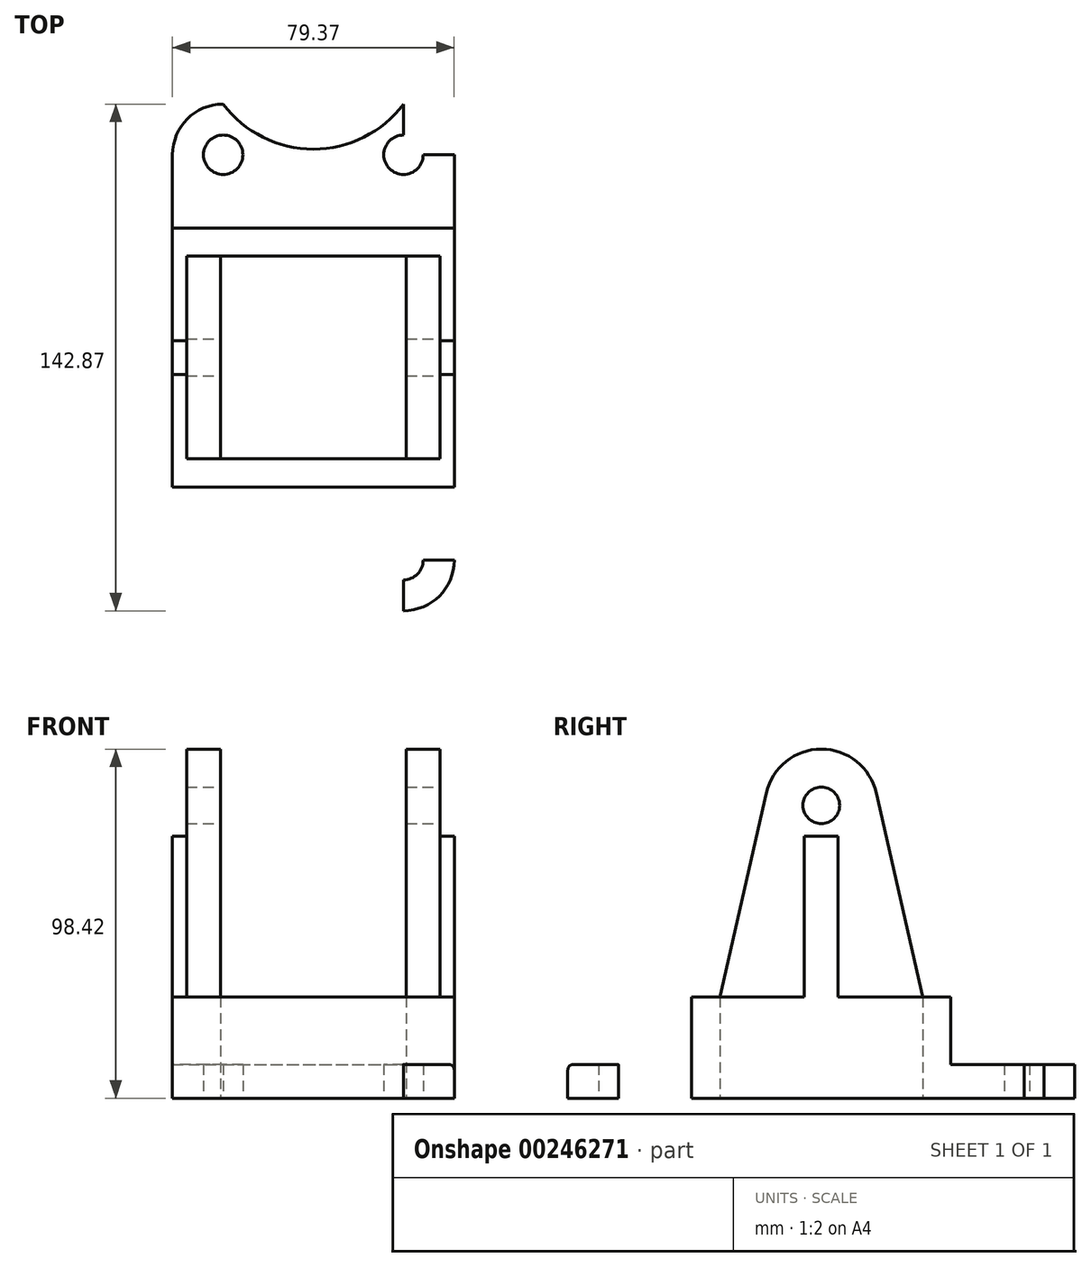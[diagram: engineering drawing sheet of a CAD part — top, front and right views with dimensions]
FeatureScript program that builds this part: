
annotation { "Feature Type Name" : "Feature", "Feature Type Description" : "" }
export const myFeature = defineFeature(function(context is Context, id is Id, definition is map)
    precondition{}
    {
        {
            var Q0;
            Q0=qCreatedBy(makeId("Top.planeOp"),FACE);
            var sketch = newSketch(context, id + "F0", { "sketchPlane" : qUnion([Q0])});
            skArc(sketch, "E0", {"start": v(-23.97, 73.31) * mm, "mid": v(-34.08, 69.13) * mm, "end": v(-38.26, 59.03) * mm});
            skLineSegment(sketch, "E1", {"start": v(-23.97, 59.03) * mm, "end": v(-23.97, 73.31) * mm, "construction": true});
            skLineSegment(sketch, "E2", {"start": v(-23.97, 59.03) * mm, "end": v(-38.26, 59.03) * mm, "construction": true});
            skLineSegment(sketch, "E3", {"start": v(-38.26, 59.03) * mm, "end": v(-38.26, -55.27) * mm});
            skLineSegment(sketch, "E4", {"start": v(-23.97, 73.31) * mm, "end": v(26.83, 73.31) * mm, "construction": true});
            skPoint(sketch, "E5", {"position": v(1.43, 73.31) * mm});
            skArc(sketch, "E6", {"start": v(-23.97, 73.31) * mm, "mid": v(1.43, 60.61) * mm, "end": v(26.83, 73.31) * mm});
            skCircle(sketch, "E7", {"center": v(-23.97, 59.03) * mm, "radius": 5.56 * mm});
            skPoint(sketch, "E8", {"position": v(-38.26, 1.88) * mm});
            skLineSegment(sketch, "E9.MirrorCS", {"start": v(-23.97, -69.56) * mm, "end": v(26.83, -69.56) * mm, "construction": true});
            skArc(sketch, "E10.MirrorCS", {"start": v(-23.97, -69.56) * mm, "mid": v(1.43, -56.86) * mm, "end": v(26.83, -69.56) * mm});
            skArc(sketch, "E11.MirrorC", {"start": v(-23.97, -69.56) * mm, "mid": v(-34.08, -65.38) * mm, "end": v(-38.26, -55.27) * mm});
            skLineSegment(sketch, "E12.MirrorCS", {"start": v(-23.97, -55.27) * mm, "end": v(-38.26, -55.27) * mm, "construction": true});
            skCircle(sketch, "E13.MirrorC", {"center": v(-23.97, -55.27) * mm, "radius": 5.56 * mm});
            skLineSegment(sketch, "E14.MirrorCS", {"start": v(-23.97, -55.27) * mm, "end": v(-23.97, -69.56) * mm, "construction": true});
            skPoint(sketch, "E15.MirrorP", {"position": v(1.43, -69.56) * mm});
            skLineSegment(sketch, "E16", {"start": v(-38.26, 1.88) * mm, "end": v(-34.3, 1.88) * mm, "construction": true});
            skLineSegment(sketch, "E17", {"start": v(-34.3, 6.64) * mm, "end": v(-34.3, -2.89) * mm});
            skPoint(sketch, "E18", {"position": v(-34.3, 1.88) * mm});
            skLineSegment(sketch, "E19", {"start": v(-34.3, 6.64) * mm, "end": v(-38.26, 6.64) * mm});
            skLineSegment(sketch, "E20", {"start": v(-34.3, -2.89) * mm, "end": v(-38.26, -2.89) * mm});
            skLineSegment(sketch, "E21", {"start": v(1.43, 73.31) * mm, "end": v(1.43, -69.56) * mm, "construction": true});
            skLineSegment(sketch, "E22", {"start": v(-34.3, 1.88) * mm, "end": v(-34.3, 30.45) * mm, "construction": true});
            skLineSegment(sketch, "E23", {"start": v(-38.26, 30.45) * mm, "end": v(1.43, 30.45) * mm});
            skLineSegment(sketch, "E24", {"start": v(-38.26, 38.39) * mm, "end": v(1.43, 38.39) * mm});
            skLineSegment(sketch, "E25.MirrorCS", {"start": v(37.14, -2.89) * mm, "end": v(41.11, -2.89) * mm});
            skLineSegment(sketch, "E26.MirrorCS", {"start": v(41.11, 1.88) * mm, "end": v(37.14, 1.88) * mm, "construction": true});
            skLineSegment(sketch, "E27.MirrorCS", {"start": v(37.14, 6.64) * mm, "end": v(37.14, -2.89) * mm});
            skLineSegment(sketch, "E28.MirrorCS", {"start": v(37.14, 6.64) * mm, "end": v(41.11, 6.64) * mm});
            skLineSegment(sketch, "E29.MirrorCS", {"start": v(37.14, 1.88) * mm, "end": v(37.14, 30.45) * mm, "construction": true});
            skCircle(sketch, "E30.MirrorC", {"center": v(26.83, -55.27) * mm, "radius": 5.56 * mm});
            skLineSegment(sketch, "E31.MirrorCS", {"start": v(26.83, -55.27) * mm, "end": v(41.11, -55.27) * mm});
            skLineSegment(sketch, "E32.MirrorCS", {"start": v(41.11, 38.39) * mm, "end": v(1.43, 38.39) * mm});
            skCircle(sketch, "E33.MirrorC", {"center": v(26.83, 59.03) * mm, "radius": 5.56 * mm});
            skArc(sketch, "E34.MirrorCS", {"start": v(26.83, -69.56) * mm, "mid": v(36.93, -65.38) * mm, "end": v(41.11, -55.27) * mm});
            skLineSegment(sketch, "E35.MirrorCS", {"start": v(41.11, 30.45) * mm, "end": v(1.43, 30.45) * mm});
            skPoint(sketch, "E36.MirrorP", {"position": v(41.11, 1.88) * mm});
            skLineSegment(sketch, "E37.MirrorCS", {"start": v(26.83, -55.27) * mm, "end": v(26.83, -69.56) * mm});
            skPoint(sketch, "E38.MirrorP", {"position": v(37.14, 1.88) * mm});
            skArc(sketch, "E39.MirrorCS", {"start": v(26.83, 73.31) * mm, "mid": v(36.93, 69.13) * mm, "end": v(41.11, 59.03) * mm});
            skLineSegment(sketch, "E40.MirrorCS", {"start": v(26.83, 59.03) * mm, "end": v(26.83, 73.31) * mm});
            skLineSegment(sketch, "E41.MirrorCS", {"start": v(26.83, 59.03) * mm, "end": v(41.11, 59.03) * mm});
            skLineSegment(sketch, "E42.MirrorCS", {"start": v(41.11, 59.03) * mm, "end": v(41.11, -55.27) * mm});
            skLineSegment(sketch, "E43", {"start": v(-34.3, -2.89) * mm, "end": v(-34.3, -26.7) * mm, "construction": true});
            skLineSegment(sketch, "E44", {"start": v(-38.26, -26.7) * mm, "end": v(41.11, -26.7) * mm});
            skLineSegment(sketch, "E45", {"start": v(-38.26, -34.64) * mm, "end": v(41.11, -34.64) * mm});
            skLineSegment(sketch, "E46", {"start": v(-34.3, 38.39) * mm, "end": v(-34.3, -34.64) * mm});
            skLineSegment(sketch, "E47", {"start": v(-24.77, 38.39) * mm, "end": v(-24.77, -34.64) * mm});
            skLineSegment(sketch, "E48", {"start": v(37.14, 38.39) * mm, "end": v(37.14, -34.64) * mm});
            skLineSegment(sketch, "E49", {"start": v(27.62, 38.39) * mm, "end": v(27.62, -34.64) * mm});
            skSolve(sketch);
        }
        {
            var Q0;
            {var subQ1=sQuery(id+"F0.wireOp",EDGE,"E23");var subQ5=sQuery(id+"F0.wireOp",EDGE,"E3");var subQ7=makeQuery(id+"F0.imprint","INTERSECT",VERTEX,{"derivedFrom":[subQ5,subQ1]});Q0=makeQuery(id+"F0.imprint","IMPRINT",FACE,{"disambiguationData":[TD([[makeQuery(id+"F0.imprint","IMPRINT",EDGE,{"disambiguationData":[TD([[subQ7,1.0]])],"derivedFrom":subQ5}),1.0]])]});}
            var Q1;
            {var subQ5=sQuery(id+"F0.wireOp",EDGE,"E19");Q1=makeQuery(id+"F0.imprint","IMPRINT",FACE,{"disambiguationData":[TD([[makeQuery(id+"F0.imprint","IMPRINT",EDGE,{"derivedFrom":subQ5}),-1.0]])]});}
            var Q2;
            {var subQ3=sQuery(id+"F0.wireOp",EDGE,"E35.MirrorCS");var subQ7=sQuery(id+"F0.wireOp",EDGE,"E23");var subQ9=makeQuery(id+"F0.imprint","INTERSECT",VERTEX,{"derivedFrom":[subQ7,subQ3]});Q2=makeQuery(id+"F0.imprint","IMPRINT",FACE,{"disambiguationData":[TD([[makeQuery(id+"F0.imprint","IMPRINT",EDGE,{"disambiguationData":[TD([[subQ9,1.0]])],"derivedFrom":subQ7}),-1.0]])]});}
            var Q3;
            {var subQ3=sQuery(id+"F0.wireOp",EDGE,"E25.MirrorCS");Q3=makeQuery(id+"F0.imprint","IMPRINT",FACE,{"disambiguationData":[TD([[makeQuery(id+"F0.imprint","IMPRINT",EDGE,{"derivedFrom":subQ3}),-1.0]])]});}
            var Q4;
            {var subQ3=sQuery(id+"F0.wireOp",EDGE,"E20");Q4=makeQuery(id+"F0.imprint","IMPRINT",FACE,{"disambiguationData":[TD([[makeQuery(id+"F0.imprint","IMPRINT",EDGE,{"derivedFrom":subQ3}),1.0]])]});}
            var Q5;
            {var subQ1=sQuery(id+"F0.wireOp",EDGE,"E44");var subQ5=sQuery(id+"F0.wireOp",EDGE,"E3");var subQ7=makeQuery(id+"F0.imprint","INTERSECT",VERTEX,{"derivedFrom":[subQ5,subQ1]});Q5=makeQuery(id+"F0.imprint","IMPRINT",FACE,{"disambiguationData":[TD([[makeQuery(id+"F0.imprint","IMPRINT",EDGE,{"disambiguationData":[TD([[subQ7,-1.0]])],"derivedFrom":subQ5}),1.0]])]});}
            var Q6;
            {var subQ3=sQuery(id+"F0.wireOp",EDGE,"E28.MirrorCS");Q6=makeQuery(id+"F0.imprint","IMPRINT",FACE,{"disambiguationData":[TD([[makeQuery(id+"F0.imprint","IMPRINT",EDGE,{"derivedFrom":subQ3}),1.0]])]});}
            var Q7;
            {var subQ0=sQuery(id+"F0.wireOp",EDGE,"E42.MirrorCS");var subQ3=sQuery(id+"F0.wireOp",EDGE,"E32.MirrorCS");var subQ4=makeQuery(id+"F0.imprint","INTERSECT",VERTEX,{"derivedFrom":[subQ3,subQ0]});Q7=makeQuery(id+"F0.imprint","IMPRINT",FACE,{"disambiguationData":[TD([[makeQuery(id+"F0.imprint","IMPRINT",EDGE,{"disambiguationData":[TD([[subQ4,-1.0]])],"derivedFrom":subQ3}),1.0]])]});}
            var Q8;
            {var subQ1=sQuery(id+"F0.wireOp",EDGE,"E44");var subQ5=sQuery(id+"F0.wireOp",EDGE,"E46");var subQ6=makeQuery(id+"F0.imprint","INTERSECT",VERTEX,{"derivedFrom":[subQ1,subQ5]});Q8=makeQuery(id+"F0.imprint","IMPRINT",FACE,{"disambiguationData":[TD([[makeQuery(id+"F0.imprint","IMPRINT",EDGE,{"disambiguationData":[TD([[subQ6,-1.0]])],"derivedFrom":subQ1}),-1.0]])]});}
            var Q9;
            {var subQ1=sQuery(id+"F0.wireOp",EDGE,"E44");var subQ5=sQuery(id+"F0.wireOp",EDGE,"E47");var subQ6=makeQuery(id+"F0.imprint","INTERSECT",VERTEX,{"derivedFrom":[subQ1,subQ5]});Q9=makeQuery(id+"F0.imprint","IMPRINT",FACE,{"disambiguationData":[TD([[makeQuery(id+"F0.imprint","IMPRINT",EDGE,{"disambiguationData":[TD([[subQ6,-1.0]])],"derivedFrom":subQ1}),-1.0]])]});}
            var Q10;
            {var subQ3=sQuery(id+"F0.wireOp",EDGE,"E32.MirrorCS");var subQ5=sQuery(id+"F0.wireOp",EDGE,"E48");var subQ7=makeQuery(id+"F0.imprint","INTERSECT",VERTEX,{"derivedFrom":[subQ3,subQ5]});Q10=makeQuery(id+"F0.imprint","IMPRINT",FACE,{"disambiguationData":[TD([[makeQuery(id+"F0.imprint","IMPRINT",EDGE,{"disambiguationData":[TD([[subQ7,-1.0]])],"derivedFrom":subQ3}),1.0]])]});}
            var Q11;
            {var subQ3=sQuery(id+"F0.wireOp",EDGE,"E42.MirrorCS");var subQ5=sQuery(id+"F0.wireOp",EDGE,"E44");var subQ7=makeQuery(id+"F0.imprint","INTERSECT",VERTEX,{"derivedFrom":[subQ3,subQ5]});Q11=makeQuery(id+"F0.imprint","IMPRINT",FACE,{"disambiguationData":[TD([[makeQuery(id+"F0.imprint","IMPRINT",EDGE,{"disambiguationData":[TD([[subQ7,-1.0]])],"derivedFrom":subQ3}),-1.0]])]});}
            var Q12;
            {var subQ0=sQuery(id+"F0.wireOp",EDGE,"E49");var subQ1=sQuery(id+"F0.wireOp",EDGE,"E44");var subQ2=makeQuery(id+"F0.imprint","INTERSECT",VERTEX,{"derivedFrom":[subQ1,subQ0]});Q12=makeQuery(id+"F0.imprint","IMPRINT",FACE,{"disambiguationData":[TD([[makeQuery(id+"F0.imprint","IMPRINT",EDGE,{"disambiguationData":[TD([[subQ2,-1.0]])],"derivedFrom":subQ1}),-1.0]])]});}
            var Q13;
            {var subQ1=sQuery(id+"F0.wireOp",EDGE,"E23");var subQ5=sQuery(id+"F0.wireOp",EDGE,"E46");var subQ6=makeQuery(id+"F0.imprint","INTERSECT",VERTEX,{"derivedFrom":[subQ1,subQ5]});Q13=makeQuery(id+"F0.imprint","IMPRINT",FACE,{"disambiguationData":[TD([[makeQuery(id+"F0.imprint","IMPRINT",EDGE,{"disambiguationData":[TD([[subQ6,-1.0]])],"derivedFrom":subQ1}),1.0]])]});}
            var Q14;
            {var subQ3=sQuery(id+"F0.wireOp",EDGE,"E35.MirrorCS");var subQ5=sQuery(id+"F0.wireOp",EDGE,"E48");var subQ9=makeQuery(id+"F0.imprint","INTERSECT",VERTEX,{"derivedFrom":[subQ3,subQ5]});Q14=makeQuery(id+"F0.imprint","IMPRINT",FACE,{"disambiguationData":[TD([[makeQuery(id+"F0.imprint","IMPRINT",EDGE,{"disambiguationData":[TD([[subQ9,-1.0]])],"derivedFrom":subQ3}),1.0]])]});}
            var Q15;
            {var subQ3=sQuery(id+"F0.wireOp",EDGE,"E23");var subQ5=sQuery(id+"F0.wireOp",EDGE,"E46");var subQ9=makeQuery(id+"F0.imprint","INTERSECT",VERTEX,{"derivedFrom":[subQ3,subQ5]});Q15=makeQuery(id+"F0.imprint","IMPRINT",FACE,{"disambiguationData":[TD([[makeQuery(id+"F0.imprint","IMPRINT",EDGE,{"disambiguationData":[TD([[subQ9,-1.0]])],"derivedFrom":subQ3}),-1.0]])]});}
            var Q16;
            {var subQ1=sQuery(id+"F0.wireOp",EDGE,"E35.MirrorCS");var subQ6=sQuery(id+"F0.wireOp",EDGE,"E23");var subQ10=makeQuery(id+"F0.imprint","INTERSECT",VERTEX,{"derivedFrom":[subQ6,subQ1]});Q16=makeQuery(id+"F0.imprint","IMPRINT",FACE,{"disambiguationData":[TD([[makeQuery(id+"F0.imprint","IMPRINT",EDGE,{"disambiguationData":[TD([[subQ10,1.0]])],"derivedFrom":subQ6}),1.0]])]});}
            var Q17;
            {var subQ19=sQuery(id+"F0.wireOp",EDGE,"E0");Q17=makeQuery(id+"F0.imprint","IMPRINT",FACE,{"disambiguationData":[TD([[makeQuery(id+"F0.imprint","IMPRINT",EDGE,{"derivedFrom":subQ19}),1.0]])]});}
            var Q18;
            {var subQ3=sQuery(id+"F0.wireOp",EDGE,"E39.MirrorCS");Q18=makeQuery(id+"F0.imprint","IMPRINT",FACE,{"disambiguationData":[TD([[makeQuery(id+"F0.imprint","IMPRINT",EDGE,{"derivedFrom":subQ3}),-1.0]])]});}
            var Q19;
            {var subQ10=sQuery(id+"F0.wireOp",EDGE,"E10.MirrorCS");Q19=makeQuery(id+"F0.imprint","IMPRINT",FACE,{"disambiguationData":[TD([[makeQuery(id+"F0.imprint","IMPRINT",EDGE,{"derivedFrom":subQ10}),1.0]])]});}
            var Q20;
            {var subQ3=sQuery(id+"F0.wireOp",EDGE,"E34.MirrorCS");Q20=makeQuery(id+"F0.imprint","IMPRINT",FACE,{"disambiguationData":[TD([[makeQuery(id+"F0.imprint","IMPRINT",EDGE,{"derivedFrom":subQ3}),1.0]])]});}
            extrude(context, id + "F1", {"entities" : qUnion([Q0, Q1, Q2, Q3, Q4, Q5, Q6, Q7, Q8, Q9, Q10, Q11, Q12, Q13, Q14, Q15, Q16, Q17, Q18, Q19, Q20]), "depth" : 9.52 * mm});
        }
        {
            var Q0;
            {var subQ0=sQuery(id+"F0.wireOp",EDGE,"E42.MirrorCS");var subQ3=sQuery(id+"F0.wireOp",EDGE,"E32.MirrorCS");var subQ4=makeQuery(id+"F0.imprint","INTERSECT",VERTEX,{"derivedFrom":[subQ3,subQ0]});Q0=makeQuery(id+"F0.imprint","IMPRINT",FACE,{"disambiguationData":[TD([[makeQuery(id+"F0.imprint","IMPRINT",EDGE,{"disambiguationData":[TD([[subQ4,-1.0]])],"derivedFrom":subQ3}),1.0]])]});}
            var Q1;
            {var subQ3=sQuery(id+"F0.wireOp",EDGE,"E32.MirrorCS");var subQ5=sQuery(id+"F0.wireOp",EDGE,"E48");var subQ7=makeQuery(id+"F0.imprint","INTERSECT",VERTEX,{"derivedFrom":[subQ3,subQ5]});Q1=makeQuery(id+"F0.imprint","IMPRINT",FACE,{"disambiguationData":[TD([[makeQuery(id+"F0.imprint","IMPRINT",EDGE,{"disambiguationData":[TD([[subQ7,-1.0]])],"derivedFrom":subQ3}),1.0]])]});}
            var Q2;
            {var subQ1=sQuery(id+"F0.wireOp",EDGE,"E35.MirrorCS");var subQ6=sQuery(id+"F0.wireOp",EDGE,"E23");var subQ10=makeQuery(id+"F0.imprint","INTERSECT",VERTEX,{"derivedFrom":[subQ6,subQ1]});Q2=makeQuery(id+"F0.imprint","IMPRINT",FACE,{"disambiguationData":[TD([[makeQuery(id+"F0.imprint","IMPRINT",EDGE,{"disambiguationData":[TD([[subQ10,1.0]])],"derivedFrom":subQ6}),1.0]])]});}
            var Q3;
            {var subQ1=sQuery(id+"F0.wireOp",EDGE,"E23");var subQ5=sQuery(id+"F0.wireOp",EDGE,"E46");var subQ6=makeQuery(id+"F0.imprint","INTERSECT",VERTEX,{"derivedFrom":[subQ1,subQ5]});Q3=makeQuery(id+"F0.imprint","IMPRINT",FACE,{"disambiguationData":[TD([[makeQuery(id+"F0.imprint","IMPRINT",EDGE,{"disambiguationData":[TD([[subQ6,-1.0]])],"derivedFrom":subQ1}),1.0]])]});}
            var Q4;
            {var subQ1=sQuery(id+"F0.wireOp",EDGE,"E23");var subQ5=sQuery(id+"F0.wireOp",EDGE,"E3");var subQ7=makeQuery(id+"F0.imprint","INTERSECT",VERTEX,{"derivedFrom":[subQ5,subQ1]});Q4=makeQuery(id+"F0.imprint","IMPRINT",FACE,{"disambiguationData":[TD([[makeQuery(id+"F0.imprint","IMPRINT",EDGE,{"disambiguationData":[TD([[subQ7,1.0]])],"derivedFrom":subQ5}),1.0]])]});}
            var Q5;
            {var subQ3=sQuery(id+"F0.wireOp",EDGE,"E42.MirrorCS");var subQ5=sQuery(id+"F0.wireOp",EDGE,"E44");var subQ7=makeQuery(id+"F0.imprint","INTERSECT",VERTEX,{"derivedFrom":[subQ3,subQ5]});Q5=makeQuery(id+"F0.imprint","IMPRINT",FACE,{"disambiguationData":[TD([[makeQuery(id+"F0.imprint","IMPRINT",EDGE,{"disambiguationData":[TD([[subQ7,-1.0]])],"derivedFrom":subQ3}),-1.0]])]});}
            var Q6;
            {var subQ0=sQuery(id+"F0.wireOp",EDGE,"E49");var subQ1=sQuery(id+"F0.wireOp",EDGE,"E44");var subQ2=makeQuery(id+"F0.imprint","INTERSECT",VERTEX,{"derivedFrom":[subQ1,subQ0]});Q6=makeQuery(id+"F0.imprint","IMPRINT",FACE,{"disambiguationData":[TD([[makeQuery(id+"F0.imprint","IMPRINT",EDGE,{"disambiguationData":[TD([[subQ2,-1.0]])],"derivedFrom":subQ1}),-1.0]])]});}
            var Q7;
            {var subQ1=sQuery(id+"F0.wireOp",EDGE,"E44");var subQ5=sQuery(id+"F0.wireOp",EDGE,"E47");var subQ6=makeQuery(id+"F0.imprint","INTERSECT",VERTEX,{"derivedFrom":[subQ1,subQ5]});Q7=makeQuery(id+"F0.imprint","IMPRINT",FACE,{"disambiguationData":[TD([[makeQuery(id+"F0.imprint","IMPRINT",EDGE,{"disambiguationData":[TD([[subQ6,-1.0]])],"derivedFrom":subQ1}),-1.0]])]});}
            var Q8;
            {var subQ1=sQuery(id+"F0.wireOp",EDGE,"E44");var subQ5=sQuery(id+"F0.wireOp",EDGE,"E46");var subQ6=makeQuery(id+"F0.imprint","INTERSECT",VERTEX,{"derivedFrom":[subQ1,subQ5]});Q8=makeQuery(id+"F0.imprint","IMPRINT",FACE,{"disambiguationData":[TD([[makeQuery(id+"F0.imprint","IMPRINT",EDGE,{"disambiguationData":[TD([[subQ6,-1.0]])],"derivedFrom":subQ1}),-1.0]])]});}
            var Q9;
            {var subQ1=sQuery(id+"F0.wireOp",EDGE,"E44");var subQ5=sQuery(id+"F0.wireOp",EDGE,"E3");var subQ7=makeQuery(id+"F0.imprint","INTERSECT",VERTEX,{"derivedFrom":[subQ5,subQ1]});Q9=makeQuery(id+"F0.imprint","IMPRINT",FACE,{"disambiguationData":[TD([[makeQuery(id+"F0.imprint","IMPRINT",EDGE,{"disambiguationData":[TD([[subQ7,-1.0]])],"derivedFrom":subQ5}),1.0]])]});}
            var Q10;
            {var subQ5=sQuery(id+"F0.wireOp",EDGE,"E19");Q10=makeQuery(id+"F0.imprint","IMPRINT",FACE,{"disambiguationData":[TD([[makeQuery(id+"F0.imprint","IMPRINT",EDGE,{"derivedFrom":subQ5}),-1.0]])]});}
            var Q11;
            {var subQ3=sQuery(id+"F0.wireOp",EDGE,"E20");Q11=makeQuery(id+"F0.imprint","IMPRINT",FACE,{"disambiguationData":[TD([[makeQuery(id+"F0.imprint","IMPRINT",EDGE,{"derivedFrom":subQ3}),1.0]])]});}
            var Q12;
            {var subQ3=sQuery(id+"F0.wireOp",EDGE,"E28.MirrorCS");Q12=makeQuery(id+"F0.imprint","IMPRINT",FACE,{"disambiguationData":[TD([[makeQuery(id+"F0.imprint","IMPRINT",EDGE,{"derivedFrom":subQ3}),1.0]])]});}
            var Q13;
            {var subQ3=sQuery(id+"F0.wireOp",EDGE,"E25.MirrorCS");Q13=makeQuery(id+"F0.imprint","IMPRINT",FACE,{"disambiguationData":[TD([[makeQuery(id+"F0.imprint","IMPRINT",EDGE,{"derivedFrom":subQ3}),-1.0]])]});}
            var Q14;
            {var subQ3=sQuery(id+"F0.wireOp",EDGE,"E35.MirrorCS");var subQ5=sQuery(id+"F0.wireOp",EDGE,"E48");var subQ9=makeQuery(id+"F0.imprint","INTERSECT",VERTEX,{"derivedFrom":[subQ3,subQ5]});Q14=makeQuery(id+"F0.imprint","IMPRINT",FACE,{"disambiguationData":[TD([[makeQuery(id+"F0.imprint","IMPRINT",EDGE,{"disambiguationData":[TD([[subQ9,-1.0]])],"derivedFrom":subQ3}),1.0]])]});}
            var Q15;
            {var subQ3=sQuery(id+"F0.wireOp",EDGE,"E23");var subQ5=sQuery(id+"F0.wireOp",EDGE,"E46");var subQ9=makeQuery(id+"F0.imprint","INTERSECT",VERTEX,{"derivedFrom":[subQ3,subQ5]});Q15=makeQuery(id+"F0.imprint","IMPRINT",FACE,{"disambiguationData":[TD([[makeQuery(id+"F0.imprint","IMPRINT",EDGE,{"disambiguationData":[TD([[subQ9,-1.0]])],"derivedFrom":subQ3}),-1.0]])]});}
            extrude(context, id + "F2", {"entities" : qUnion([Q0, Q1, Q2, Q3, Q4, Q5, Q6, Q7, Q8, Q9, Q10, Q11, Q12, Q13, Q14, Q15]), "operationType" : NewBodyOperationType.ADD, "depth" : 28.57 * mm});
        }
        {
            var Q0;
            Q0=makeQuery(id+"F2.boolean.opBoolean","SPLIT",FACE,{"disambiguationData":[TD([makeQuery(id+"F2.opExtrude","SWEPT_FACE",FACE,{"disambiguationData":[OSD([sQuery(id+"F0.wireOp",EDGE,"E44")])]})])],"derivedFrom":makeQuery(id+"F1.opExtrude","CAP_FACE",FACE,{"disambiguationData":[OSD([sQuery(id+"F0.wireOp",EDGE,"E0"),sQuery(id+"F0.wireOp",EDGE,"E3"),sQuery(id+"F0.wireOp",EDGE,"E6"),sQuery(id+"F0.wireOp",EDGE,"E7"),sQuery(id+"F0.wireOp",EDGE,"E10.MirrorCS"),sQuery(id+"F0.wireOp",EDGE,"E11.MirrorC"),sQuery(id+"F0.wireOp",EDGE,"E13.MirrorC"),sQuery(id+"F0.wireOp",EDGE,"E30.MirrorC"),sQuery(id+"F0.wireOp",EDGE,"E33.MirrorC"),sQuery(id+"F0.wireOp",EDGE,"E34.MirrorCS"),sQuery(id+"F0.wireOp",EDGE,"E39.MirrorCS"),sQuery(id+"F0.wireOp",EDGE,"E42.MirrorCS")])],"isStart":false})});
            extrude(context, id + "F3", {"entities" : qUnion([Q0]), "operationType" : NewBodyOperationType.REMOVE, "oppositeDirection" : true, "depth" : 25.4 * mm});
        }
        {
            var Q0;
            {var subQ2=sQuery(id+"F0.wireOp",EDGE,"E19");Q0=makeQuery(id+"F0.imprint","IMPRINT",FACE,{"disambiguationData":[TD([[makeQuery(id+"F0.imprint","IMPRINT",EDGE,{"derivedFrom":subQ2}),1.0]])]});}
            var Q1;
            {var subQ2=sQuery(id+"F0.wireOp",EDGE,"E25.MirrorCS");Q1=makeQuery(id+"F0.imprint","IMPRINT",FACE,{"disambiguationData":[TD([[makeQuery(id+"F0.imprint","IMPRINT",EDGE,{"derivedFrom":subQ2}),1.0]])]});}
            extrude(context, id + "F4", {"entities" : qUnion([Q0, Q1]), "operationType" : NewBodyOperationType.ADD, "depth" : 73.82 * mm});
        }
        {
            var Q0;
            Q0=makeQuery(id+"F2.opExtrude","CAP_FACE",FACE,{"disambiguationData":[OSD([sQuery(id+"F0.wireOp",EDGE,"E3"),sQuery(id+"F0.wireOp",EDGE,"E19"),sQuery(id+"F0.wireOp",EDGE,"E20"),sQuery(id+"F0.wireOp",EDGE,"E23"),sQuery(id+"F0.wireOp",EDGE,"E24"),sQuery(id+"F0.wireOp",EDGE,"E25.MirrorCS"),sQuery(id+"F0.wireOp",EDGE,"E28.MirrorCS"),sQuery(id+"F0.wireOp",EDGE,"E32.MirrorCS"),sQuery(id+"F0.wireOp",EDGE,"E35.MirrorCS"),sQuery(id+"F0.wireOp",EDGE,"E42.MirrorCS"),sQuery(id+"F0.wireOp",EDGE,"E44"),sQuery(id+"F0.wireOp",EDGE,"E45"),sQuery(id+"F0.wireOp",EDGE,"E46"),sQuery(id+"F0.wireOp",EDGE,"E47"),sQuery(id+"F0.wireOp",EDGE,"E48"),sQuery(id+"F0.wireOp",EDGE,"E49")])],"isStart":false});
            cPlane(context, id + "F5", {"entities" : qUnion([Q0]), "cplaneType" : CPlaneType.OFFSET, "offset" : 0 * mm, "width" : 152.4 * mm, "height" : 152.4 * mm});
        }
        {
            var Q0;
            Q0=qCreatedBy(id+"F5.planeOp",FACE);
            var sketch = newSketch(context, id + "F6", { "sketchPlane" : qUnion([Q0])});
            skLineSegment(sketch, "E50.0.0", {"start": v(37.14, 6.64) * mm, "end": v(37.14, 30.45) * mm});
            skLineSegment(sketch, "E50.0.1", {"start": v(37.14, 30.45) * mm, "end": v(27.62, 30.45) * mm});
            skLineSegment(sketch, "E50.0.2", {"start": v(27.62, 30.45) * mm, "end": v(27.62, -26.7) * mm});
            skLineSegment(sketch, "E50.0.3", {"start": v(27.62, -26.7) * mm, "end": v(37.14, -26.7) * mm});
            skLineSegment(sketch, "E50.0.4", {"start": v(37.14, -26.7) * mm, "end": v(37.14, -2.89) * mm});
            skLineSegment(sketch, "E50.0.5", {"start": v(37.14, -2.89) * mm, "end": v(37.14, 6.64) * mm});
            skLineSegment(sketch, "E51.0.0", {"start": v(-24.77, 30.45) * mm, "end": v(-34.3, 30.45) * mm});
            skLineSegment(sketch, "E51.0.1", {"start": v(-34.3, 30.45) * mm, "end": v(-34.3, 6.64) * mm});
            skLineSegment(sketch, "E51.0.2", {"start": v(-34.3, 6.64) * mm, "end": v(-34.3, -2.89) * mm});
            skLineSegment(sketch, "E51.0.3", {"start": v(-34.3, -2.89) * mm, "end": v(-34.3, -26.7) * mm});
            skLineSegment(sketch, "E51.0.4", {"start": v(-34.3, -26.7) * mm, "end": v(-24.77, -26.7) * mm});
            skLineSegment(sketch, "E51.0.5", {"start": v(-24.77, -26.7) * mm, "end": v(-24.77, 30.45) * mm});
            skSolve(sketch);
        }
        {
            var Q0;
            Q0=makeQuery(id+"F6.imprint","IMPRINT",FACE,{"disambiguationData":[TD([[makeQuery(id+"F6.imprint","IMPRINT",EDGE,{"derivedFrom":sQuery(id+"F6.wireOp",EDGE,"E51.0.0")}),1.0]])]});
            var Q1;
            Q1=makeQuery(id+"F6.imprint","IMPRINT",FACE,{"disambiguationData":[TD([[makeQuery(id+"F6.imprint","IMPRINT",EDGE,{"derivedFrom":sQuery(id+"F6.wireOp",EDGE,"E50.0.0")}),1.0]])]});
            extrude(context, id + "F7", {"entities" : qUnion([Q0, Q1]), "operationType" : NewBodyOperationType.ADD, "depth" : 69.85 * mm});
        }
        {
            var Q0;
            Q0=makeQuery(id+"F7.opExtrude","SWEPT_FACE",FACE,{"disambiguationData":[OSD([sQuery(id+"F6.wireOp",EDGE,"E50.0.0"),sQuery(id+"F6.wireOp",EDGE,"E50.0.4"),sQuery(id+"F6.wireOp",EDGE,"E50.0.5")])]});
            cPlane(context, id + "F8", {"entities" : qUnion([Q0]), "cplaneType" : CPlaneType.OFFSET, "offset" : 0 * mm, "width" : 152.4 * mm, "height" : 152.4 * mm});
        }
        {
            var Q0;
            Q0=qCreatedBy(id+"F8.planeOp",FACE);
            var sketch = newSketch(context, id + "F9", { "sketchPlane" : qUnion([Q0])});
            skLineSegment(sketch, "E52.0", {"start": v(-2.89, 28.58) * mm, "end": v(-34.64, 28.58) * mm});
            skLineSegment(sketch, "E53.0", {"start": v(38.39, 28.58) * mm, "end": v(6.64, 28.58) * mm});
            skLineSegment(sketch, "E54.0.0", {"start": v(-26.7, 28.58) * mm, "end": v(-2.89, 28.58) * mm});
            skLineSegment(sketch, "E54.0.1", {"start": v(-2.89, 28.58) * mm, "end": v(-2.89, 73.82) * mm});
            skLineSegment(sketch, "E54.0.2", {"start": v(-2.89, 73.82) * mm, "end": v(6.64, 73.82) * mm});
            skLineSegment(sketch, "E54.0.3", {"start": v(6.64, 73.82) * mm, "end": v(6.64, 28.58) * mm});
            skLineSegment(sketch, "E54.0.4", {"start": v(6.64, 28.58) * mm, "end": v(30.45, 28.58) * mm});
            skLineSegment(sketch, "E54.0.5", {"start": v(30.45, 28.58) * mm, "end": v(30.45, 98.43) * mm});
            skLineSegment(sketch, "E54.0.6", {"start": v(30.45, 98.43) * mm, "end": v(-26.7, 98.43) * mm});
            skLineSegment(sketch, "E54.0.7", {"start": v(-26.7, 98.43) * mm, "end": v(-26.7, 28.58) * mm});
            skLineSegment(sketch, "E55", {"start": v(-2.89, 28.58) * mm, "end": v(6.64, 28.58) * mm});
            skPoint(sketch, "E56", {"position": v(1.88, 28.58) * mm});
            skCircle(sketch, "E57", {"center": v(1.88, 82.55) * mm, "radius": 5.16 * mm});
            skLineSegment(sketch, "E58", {"start": v(-26.7, 28.57) * mm, "end": v(-13.6, 86.08) * mm});
            skLineSegment(sketch, "E59", {"start": v(30.45, 28.58) * mm, "end": v(17.35, 86.08) * mm});
            skArc(sketch, "E60.trimOffspring", {"start": v(17.35, 86.08) * mm, "mid": v(1.88, 98.43) * mm, "end": v(-13.6, 86.08) * mm});
            skLineSegment(sketch, "E61", {"start": v(-26.7, 28.58) * mm, "end": v(-26.7, 98.43) * mm});
            skLineSegment(sketch, "E62", {"start": v(-26.7, 98.43) * mm, "end": v(30.45, 98.43) * mm});
            skSolve(sketch);
        }
        {
            var Q0;
            {var subQ4=sQuery(id+"F9.wireOp",EDGE,"E58");Q0=makeQuery(id+"F9.imprint","IMPRINT",FACE,{"disambiguationData":[TD([[makeQuery(id+"F9.imprint","IMPRINT",EDGE,{"derivedFrom":subQ4}),1.0]])]});}
            var Q1;
            {var subQ4=sQuery(id+"F9.wireOp",EDGE,"E59");Q1=makeQuery(id+"F9.imprint","IMPRINT",FACE,{"disambiguationData":[TD([[makeQuery(id+"F9.imprint","IMPRINT",EDGE,{"derivedFrom":subQ4}),-1.0]])]});}
            var Q2;
            Q2=makeQuery(id+"F9.imprint","IMPRINT",FACE,{"disambiguationData":[TD([[makeQuery(id+"F9.imprint","IMPRINT",EDGE,{"derivedFrom":sQuery(id+"F9.wireOp",EDGE,"E57")}),1.0]])]});
            extrude(context, id + "F10", {"entities" : qUnion([Q0, Q1, Q2]), "operationType" : NewBodyOperationType.REMOVE, "oppositeDirection" : true, "depth" : 101.6 * mm});
        }
        {
            var Q0;
            Q0=makeQuery(id+"F2.opExtrude","CAP_EDGE",EDGE,{"disambiguationData":[OSD([sQuery(id+"F0.wireOp",EDGE,"E24"),sQuery(id+"F0.wireOp",EDGE,"E32.MirrorCS")])],"isStart":false});
            var Q1;
            Q1=makeQuery(id+"F4.opExtrude","SWEPT_EDGE",EDGE,{"disambiguationData":[OSD([sQuery(id+"F0.wireOp",EDGE,"E28.MirrorCS"),sQuery(id+"F0.wireOp",EDGE,"E48")])]});
            var Q2;
            {var subQ0=sQuery(id+"F6.wireOp",EDGE,"E50.0.0");var subQ1=sQuery(id+"F6.wireOp",EDGE,"E50.0.4");var subQ2=sQuery(id+"F6.wireOp",EDGE,"E50.0.5");var subQ3=sQuery(id+"F0.wireOp",EDGE,"E25.MirrorCS");Q2=makeQuery(id+"F7.boolean.opBoolean","SPLIT",EDGE,{"disambiguationData":[TD([makeQuery(id+"F4.opExtrude","SWEPT_FACE",FACE,{"disambiguationData":[OSD([subQ3])]})])],"derivedFrom":makeQuery(id+"F7.opExtrude","CAP_EDGE",EDGE,{"disambiguationData":[OSD([subQ0,subQ1,subQ2])],"isStart":true})});}
            var Q3;
            Q3=makeQuery(id+"F1.opExtrude","CAP_EDGE",EDGE,{"disambiguationData":[OSD([sQuery(id+"F0.wireOp",EDGE,"E10.MirrorCS")])],"isStart":false});
            var Q4;
            {var subQ0=sQuery(id+"F6.wireOp",EDGE,"E50.0.0");var subQ1=sQuery(id+"F6.wireOp",EDGE,"E50.0.4");var subQ2=sQuery(id+"F6.wireOp",EDGE,"E50.0.5");var subQ3=sQuery(id+"F0.wireOp",EDGE,"E28.MirrorCS");Q4=makeQuery(id+"F7.boolean.opBoolean","SPLIT",EDGE,{"disambiguationData":[TD([makeQuery(id+"F4.opExtrude","SWEPT_FACE",FACE,{"disambiguationData":[OSD([subQ3])]})])],"derivedFrom":makeQuery(id+"F7.opExtrude","CAP_EDGE",EDGE,{"disambiguationData":[OSD([subQ0,subQ1,subQ2])],"isStart":true})});}
            var Q5;
            Q5=makeQuery(id+"F1.opExtrude","CAP_EDGE",EDGE,{"disambiguationData":[OSD([sQuery(id+"F0.wireOp",EDGE,"E34.MirrorCS")])],"isStart":false});
            var Q6;
            Q6=makeQuery(id+"F1.opExtrude","CAP_EDGE",EDGE,{"disambiguationData":[OSD([sQuery(id+"F0.wireOp",EDGE,"E11.MirrorC")])],"isStart":false});
            var Q7;
            {var subQ0=sQuery(id+"F0.wireOp",EDGE,"E49");var subQ1=sQuery(id+"F9.wireOp",EDGE,"E60.trimOffspring");Q7=makeQuery(id+"F10.boolean.opBoolean","INTERSECT",EDGE,{"derivedFrom":[makeQuery(id+"F7.boolean.opBoolean","MERGE",FACE,{"derivedFrom":[makeQuery(id+"F3.boolean.opBoolean","MERGE",FACE,{"derivedFrom":[makeQuery(id+"F2.opExtrude","SWEPT_FACE",FACE,{"disambiguationData":[OSD([subQ0])]}),makeQuery(id+"F3.opExtrude","SWEPT_FACE",FACE,{"disambiguationData":[OSD([sQuery(id+"F0.wireOp",EDGE,"E0"),sQuery(id+"F0.wireOp",EDGE,"E3"),sQuery(id+"F0.wireOp",EDGE,"E6"),sQuery(id+"F0.wireOp",EDGE,"E7"),sQuery(id+"F0.wireOp",EDGE,"E10.MirrorCS"),sQuery(id+"F0.wireOp",EDGE,"E11.MirrorC"),sQuery(id+"F0.wireOp",EDGE,"E13.MirrorC"),sQuery(id+"F0.wireOp",EDGE,"E19"),sQuery(id+"F0.wireOp",EDGE,"E20"),sQuery(id+"F0.wireOp",EDGE,"E25.MirrorCS"),sQuery(id+"F0.wireOp",EDGE,"E28.MirrorCS"),sQuery(id+"F0.wireOp",EDGE,"E30.MirrorC"),sQuery(id+"F0.wireOp",EDGE,"E33.MirrorC"),sQuery(id+"F0.wireOp",EDGE,"E34.MirrorCS"),sQuery(id+"F0.wireOp",EDGE,"E39.MirrorCS"),sQuery(id+"F0.wireOp",EDGE,"E42.MirrorCS"),sQuery(id+"F0.wireOp",EDGE,"E46"),sQuery(id+"F0.wireOp",EDGE,"E48"),subQ0])]})]}),makeQuery(id+"F7.opExtrude","SWEPT_FACE",FACE,{"disambiguationData":[OSD([sQuery(id+"F6.wireOp",EDGE,"E50.0.2")])]})]}),makeQuery(id+"F10.opExtrude","SWEPT_FACE",FACE,{"disambiguationData":[OSD([subQ1]),TDD([makeQuery(id+"F9.imprint","IMPRINT",EDGE,{"disambiguationData":[TD([[makeQuery(id+"F9.imprint","INTERSECT",VERTEX,{"derivedFrom":[sQuery(id+"F9.wireOp",EDGE,"E59"),subQ1]}),-1.0]])],"derivedFrom":subQ1})])]}),makeQuery(id+"F10.opExtrude","SWEPT_FACE",FACE,{"disambiguationData":[OSD([subQ1]),TDD([makeQuery(id+"F9.imprint","IMPRINT",EDGE,{"disambiguationData":[TD([[makeQuery(id+"F9.imprint","INTERSECT",VERTEX,{"derivedFrom":[sQuery(id+"F9.wireOp",EDGE,"E58"),subQ1]}),1.0]])],"derivedFrom":subQ1})])]})]});}
            var Q8;
            {var subQ0=sQuery(id+"F0.wireOp",EDGE,"E47");Q8=makeQuery(id+"F10.boolean.opBoolean","INTERSECT",EDGE,{"derivedFrom":[makeQuery(id+"F7.boolean.opBoolean","MERGE",FACE,{"derivedFrom":[makeQuery(id+"F3.boolean.opBoolean","MERGE",FACE,{"derivedFrom":[makeQuery(id+"F2.opExtrude","SWEPT_FACE",FACE,{"disambiguationData":[OSD([subQ0])]}),makeQuery(id+"F3.opExtrude","SWEPT_FACE",FACE,{"disambiguationData":[OSD([sQuery(id+"F0.wireOp",EDGE,"E0"),sQuery(id+"F0.wireOp",EDGE,"E3"),sQuery(id+"F0.wireOp",EDGE,"E6"),sQuery(id+"F0.wireOp",EDGE,"E7"),sQuery(id+"F0.wireOp",EDGE,"E10.MirrorCS"),sQuery(id+"F0.wireOp",EDGE,"E11.MirrorC"),sQuery(id+"F0.wireOp",EDGE,"E13.MirrorC"),sQuery(id+"F0.wireOp",EDGE,"E19"),sQuery(id+"F0.wireOp",EDGE,"E20"),sQuery(id+"F0.wireOp",EDGE,"E25.MirrorCS"),sQuery(id+"F0.wireOp",EDGE,"E28.MirrorCS"),sQuery(id+"F0.wireOp",EDGE,"E30.MirrorC"),sQuery(id+"F0.wireOp",EDGE,"E33.MirrorC"),sQuery(id+"F0.wireOp",EDGE,"E34.MirrorCS"),sQuery(id+"F0.wireOp",EDGE,"E39.MirrorCS"),sQuery(id+"F0.wireOp",EDGE,"E42.MirrorCS"),sQuery(id+"F0.wireOp",EDGE,"E46"),subQ0,sQuery(id+"F0.wireOp",EDGE,"E48")])]})]}),makeQuery(id+"F7.opExtrude","SWEPT_FACE",FACE,{"disambiguationData":[OSD([sQuery(id+"F6.wireOp",EDGE,"E51.0.5")])]})]}),makeQuery(id+"F10.opExtrude","SWEPT_FACE",FACE,{"disambiguationData":[OSD([sQuery(id+"F9.wireOp",EDGE,"E59")])]})]});}
            var Q9;
            {var subQ0=sQuery(id+"F0.wireOp",EDGE,"E49");Q9=makeQuery(id+"F10.boolean.opBoolean","INTERSECT",EDGE,{"derivedFrom":[makeQuery(id+"F7.boolean.opBoolean","MERGE",FACE,{"derivedFrom":[makeQuery(id+"F3.boolean.opBoolean","MERGE",FACE,{"derivedFrom":[makeQuery(id+"F2.opExtrude","SWEPT_FACE",FACE,{"disambiguationData":[OSD([subQ0])]}),makeQuery(id+"F3.opExtrude","SWEPT_FACE",FACE,{"disambiguationData":[OSD([sQuery(id+"F0.wireOp",EDGE,"E0"),sQuery(id+"F0.wireOp",EDGE,"E3"),sQuery(id+"F0.wireOp",EDGE,"E6"),sQuery(id+"F0.wireOp",EDGE,"E7"),sQuery(id+"F0.wireOp",EDGE,"E10.MirrorCS"),sQuery(id+"F0.wireOp",EDGE,"E11.MirrorC"),sQuery(id+"F0.wireOp",EDGE,"E13.MirrorC"),sQuery(id+"F0.wireOp",EDGE,"E19"),sQuery(id+"F0.wireOp",EDGE,"E20"),sQuery(id+"F0.wireOp",EDGE,"E25.MirrorCS"),sQuery(id+"F0.wireOp",EDGE,"E28.MirrorCS"),sQuery(id+"F0.wireOp",EDGE,"E30.MirrorC"),sQuery(id+"F0.wireOp",EDGE,"E33.MirrorC"),sQuery(id+"F0.wireOp",EDGE,"E34.MirrorCS"),sQuery(id+"F0.wireOp",EDGE,"E39.MirrorCS"),sQuery(id+"F0.wireOp",EDGE,"E42.MirrorCS"),sQuery(id+"F0.wireOp",EDGE,"E46"),sQuery(id+"F0.wireOp",EDGE,"E48"),subQ0])]})]}),makeQuery(id+"F7.opExtrude","SWEPT_FACE",FACE,{"disambiguationData":[OSD([sQuery(id+"F6.wireOp",EDGE,"E50.0.2")])]})]}),makeQuery(id+"F10.opExtrude","SWEPT_FACE",FACE,{"disambiguationData":[OSD([sQuery(id+"F9.wireOp",EDGE,"E59")])]})]});}
            var Q10;
            Q10=makeQuery(id+"F2.opExtrude","CAP_EDGE",EDGE,{"disambiguationData":[OSD([sQuery(id+"F0.wireOp",EDGE,"E44")])],"isStart":false});
            var Q11;
            Q11=makeQuery(id+"F10.boolean.opBoolean","MERGE",EDGE,{"derivedFrom":[makeQuery(id+"F7.opExtrude","CAP_EDGE",EDGE,{"disambiguationData":[OSD([sQuery(id+"F6.wireOp",EDGE,"E50.0.1")])],"isStart":true}),makeQuery(id+"F10.opExtrude","SWEPT_EDGE",EDGE,{"disambiguationData":[OSD([sQuery(id+"F9.wireOp",EDGE,"E54.0.4"),sQuery(id+"F9.wireOp",EDGE,"E59"),sQuery(id+"F9.wireOp",EDGE,"E54.0.5")])]})]});
            var Q12;
            Q12=makeQuery(id+"F10.boolean.opBoolean","MERGE",EDGE,{"derivedFrom":[makeQuery(id+"F7.opExtrude","CAP_EDGE",EDGE,{"disambiguationData":[OSD([sQuery(id+"F6.wireOp",EDGE,"E50.0.3")])],"isStart":true}),makeQuery(id+"F10.opExtrude","SWEPT_EDGE",EDGE,{"disambiguationData":[OSD([sQuery(id+"F9.wireOp",EDGE,"E54.0.0"),sQuery(id+"F9.wireOp",EDGE,"E58"),sQuery(id+"F9.wireOp",EDGE,"E61")])]})]});
            var Q13;
            {var subQ0=sQuery(id+"F9.wireOp",EDGE,"E60.trimOffspring");Q13=makeQuery(id+"F10.boolean.opBoolean","TWEAK_EDGE",EDGE,{"derivedFrom":[makeQuery(id+"F10.opExtrude","CAP_EDGE",EDGE,{"disambiguationData":[OSD([subQ0]),TDD([makeQuery(id+"F9.imprint","IMPRINT",EDGE,{"disambiguationData":[TD([[makeQuery(id+"F9.imprint","INTERSECT",VERTEX,{"derivedFrom":[sQuery(id+"F9.wireOp",EDGE,"E59"),subQ0]}),-1.0]])],"derivedFrom":subQ0})])],"isStart":true}),makeQuery(id+"F10.opExtrude","CAP_EDGE",EDGE,{"disambiguationData":[OSD([subQ0]),TDD([makeQuery(id+"F9.imprint","IMPRINT",EDGE,{"disambiguationData":[TD([[makeQuery(id+"F9.imprint","INTERSECT",VERTEX,{"derivedFrom":[sQuery(id+"F9.wireOp",EDGE,"E58"),subQ0]}),1.0]])],"derivedFrom":subQ0})])],"isStart":true})]});}
            var Q14;
            Q14=makeQuery(id+"F10.boolean.opBoolean","COPY",EDGE,{"derivedFrom":makeQuery(id+"F10.opExtrude","CAP_EDGE",EDGE,{"disambiguationData":[OSD([sQuery(id+"F9.wireOp",EDGE,"E58")])],"isStart":true})});
            var Q15;
            Q15=makeQuery(id+"F10.boolean.opBoolean","COPY",EDGE,{"derivedFrom":makeQuery(id+"F10.opExtrude","CAP_EDGE",EDGE,{"disambiguationData":[OSD([sQuery(id+"F9.wireOp",EDGE,"E59")])],"isStart":true})});
            var Q16;
            {var subQ0=sQuery(id+"F0.wireOp",EDGE,"E3");var subQ1=makeQuery(id+"F0.imprint","INTERSECT",VERTEX,{"derivedFrom":[subQ0,sQuery(id+"F0.wireOp",EDGE,"E23")]});Q16=makeQuery(id+"F2.opExtrude","CAP_EDGE",EDGE,{"disambiguationData":[OSD([subQ0]),TDD([makeQuery(id+"F0.imprint","IMPRINT",EDGE,{"disambiguationData":[TD([[subQ1,1.0]])],"derivedFrom":subQ0}),makeQuery(id+"F0.imprint","IMPRINT",EDGE,{"disambiguationData":[TD([[makeQuery(id+"F0.imprint","INTERSECT",VERTEX,{"derivedFrom":[subQ0,sQuery(id+"F0.wireOp",EDGE,"E19")]}),1.0]])],"derivedFrom":subQ0})])],"isStart":false});}
            var Q17;
            {var subQ0=sQuery(id+"F9.wireOp",EDGE,"E60.trimOffspring");Q17=makeQuery(id+"F10.boolean.opBoolean","INTERSECT",EDGE,{"derivedFrom":[makeQuery(id+"F7.opExtrude","SWEPT_FACE",FACE,{"disambiguationData":[OSD([sQuery(id+"F6.wireOp",EDGE,"E51.0.1"),sQuery(id+"F6.wireOp",EDGE,"E51.0.2"),sQuery(id+"F6.wireOp",EDGE,"E51.0.3")])]}),makeQuery(id+"F10.opExtrude","SWEPT_FACE",FACE,{"disambiguationData":[OSD([subQ0]),TDD([makeQuery(id+"F9.imprint","IMPRINT",EDGE,{"disambiguationData":[TD([[makeQuery(id+"F9.imprint","INTERSECT",VERTEX,{"derivedFrom":[sQuery(id+"F9.wireOp",EDGE,"E59"),subQ0]}),-1.0]])],"derivedFrom":subQ0})])]}),makeQuery(id+"F10.opExtrude","SWEPT_FACE",FACE,{"disambiguationData":[OSD([subQ0]),TDD([makeQuery(id+"F9.imprint","IMPRINT",EDGE,{"disambiguationData":[TD([[makeQuery(id+"F9.imprint","INTERSECT",VERTEX,{"derivedFrom":[sQuery(id+"F9.wireOp",EDGE,"E58"),subQ0]}),1.0]])],"derivedFrom":subQ0})])]})]});}
            var Q18;
            Q18=makeQuery(id+"F1.opExtrude","CAP_EDGE",EDGE,{"disambiguationData":[OSD([sQuery(id+"F0.wireOp",EDGE,"E39.MirrorCS")])],"isStart":false});
            var Q19;
            Q19=makeQuery(id+"F10.boolean.opBoolean","COPY",EDGE,{"disambiguationData":[OD(0.0)],"derivedFrom":makeQuery(id+"F10.opExtrude","SWEPT_EDGE",EDGE,{"disambiguationData":[OSD([sQuery(id+"F9.wireOp",EDGE,"E58"),sQuery(id+"F9.wireOp",EDGE,"E60.trimOffspring")])]})});
            var Q20;
            Q20=makeQuery(id+"F4.opExtrude","CAP_EDGE",EDGE,{"disambiguationData":[OSD([sQuery(id+"F0.wireOp",EDGE,"E28.MirrorCS")])],"isStart":false});
            var Q21;
            Q21=makeQuery(id+"F2.opExtrude","CAP_EDGE",EDGE,{"disambiguationData":[OSD([sQuery(id+"F0.wireOp",EDGE,"E45")])],"isStart":false});
            var Q22;
            {var subQ0=sQuery(id+"F0.wireOp",EDGE,"E49");Q22=makeQuery(id+"F10.boolean.opBoolean","INTERSECT",EDGE,{"derivedFrom":[makeQuery(id+"F7.boolean.opBoolean","MERGE",FACE,{"derivedFrom":[makeQuery(id+"F3.boolean.opBoolean","MERGE",FACE,{"derivedFrom":[makeQuery(id+"F2.opExtrude","SWEPT_FACE",FACE,{"disambiguationData":[OSD([subQ0])]}),makeQuery(id+"F3.opExtrude","SWEPT_FACE",FACE,{"disambiguationData":[OSD([sQuery(id+"F0.wireOp",EDGE,"E0"),sQuery(id+"F0.wireOp",EDGE,"E3"),sQuery(id+"F0.wireOp",EDGE,"E6"),sQuery(id+"F0.wireOp",EDGE,"E7"),sQuery(id+"F0.wireOp",EDGE,"E10.MirrorCS"),sQuery(id+"F0.wireOp",EDGE,"E11.MirrorC"),sQuery(id+"F0.wireOp",EDGE,"E13.MirrorC"),sQuery(id+"F0.wireOp",EDGE,"E19"),sQuery(id+"F0.wireOp",EDGE,"E20"),sQuery(id+"F0.wireOp",EDGE,"E25.MirrorCS"),sQuery(id+"F0.wireOp",EDGE,"E28.MirrorCS"),sQuery(id+"F0.wireOp",EDGE,"E30.MirrorC"),sQuery(id+"F0.wireOp",EDGE,"E33.MirrorC"),sQuery(id+"F0.wireOp",EDGE,"E34.MirrorCS"),sQuery(id+"F0.wireOp",EDGE,"E39.MirrorCS"),sQuery(id+"F0.wireOp",EDGE,"E42.MirrorCS"),sQuery(id+"F0.wireOp",EDGE,"E46"),sQuery(id+"F0.wireOp",EDGE,"E48"),subQ0])]})]}),makeQuery(id+"F7.opExtrude","SWEPT_FACE",FACE,{"disambiguationData":[OSD([sQuery(id+"F6.wireOp",EDGE,"E50.0.2")])]})]}),makeQuery(id+"F10.opExtrude","SWEPT_FACE",FACE,{"disambiguationData":[OSD([sQuery(id+"F9.wireOp",EDGE,"E58")])]})]});}
            var Q23;
            Q23=makeQuery(id+"F1.opExtrude","CAP_EDGE",EDGE,{"disambiguationData":[OSD([sQuery(id+"F0.wireOp",EDGE,"E6")])],"isStart":false});
            var Q24;
            Q24=makeQuery(id+"F2.opExtrude","SWEPT_EDGE",EDGE,{"disambiguationData":[OSD([sQuery(id+"F0.wireOp",EDGE,"E32.MirrorCS"),sQuery(id+"F0.wireOp",EDGE,"E42.MirrorCS")])]});
            var Q25;
            Q25=makeQuery(id+"F4.opExtrude","CAP_EDGE",EDGE,{"disambiguationData":[OSD([sQuery(id+"F0.wireOp",EDGE,"E42.MirrorCS")])],"isStart":false});
            var Q26;
            Q26=makeQuery(id+"F10.boolean.opBoolean","INTERSECT",EDGE,{"derivedFrom":[makeQuery(id+"F7.opExtrude","SWEPT_FACE",FACE,{"disambiguationData":[OSD([sQuery(id+"F6.wireOp",EDGE,"E51.0.1"),sQuery(id+"F6.wireOp",EDGE,"E51.0.2"),sQuery(id+"F6.wireOp",EDGE,"E51.0.3")])]}),makeQuery(id+"F10.opExtrude","SWEPT_FACE",FACE,{"disambiguationData":[OSD([sQuery(id+"F9.wireOp",EDGE,"E59")])]})]});
            var Q27;
            {var subQ0=sQuery(id+"F0.wireOp",EDGE,"E42.MirrorCS");var subQ1=makeQuery(id+"F0.imprint","INTERSECT",VERTEX,{"derivedFrom":[sQuery(id+"F0.wireOp",EDGE,"E32.MirrorCS"),subQ0]});Q27=makeQuery(id+"F1.opExtrude","CAP_EDGE",EDGE,{"disambiguationData":[OSD([subQ0]),TDD([makeQuery(id+"F0.imprint","IMPRINT",EDGE,{"disambiguationData":[TD([[subQ1,1.0]])],"derivedFrom":subQ0}),makeQuery(id+"F0.imprint","IMPRINT",EDGE,{"disambiguationData":[TD([[subQ1,-1.0]])],"derivedFrom":subQ0}),makeQuery(id+"F0.imprint","IMPRINT",EDGE,{"disambiguationData":[TD([[makeQuery(id+"F0.imprint","INTERSECT",VERTEX,{"derivedFrom":[sQuery(id+"F0.wireOp",EDGE,"E28.MirrorCS"),subQ0]}),1.0]])],"derivedFrom":subQ0})])],"isStart":false});}
            var Q28;
            {var subQ0=sQuery(id+"F0.wireOp",EDGE,"E42.MirrorCS");var subQ1=makeQuery(id+"F0.imprint","INTERSECT",VERTEX,{"derivedFrom":[subQ0,sQuery(id+"F0.wireOp",EDGE,"E44")]});var subQ2=makeQuery(id+"F0.imprint","INTERSECT",VERTEX,{"derivedFrom":[subQ0,sQuery(id+"F0.wireOp",EDGE,"E45")]});Q28=makeQuery(id+"F1.opExtrude","CAP_EDGE",EDGE,{"disambiguationData":[OSD([subQ0]),TDD([makeQuery(id+"F0.imprint","IMPRINT",EDGE,{"disambiguationData":[TD([[makeQuery(id+"F0.imprint","INTERSECT",VERTEX,{"derivedFrom":[sQuery(id+"F0.wireOp",EDGE,"E25.MirrorCS"),subQ0]}),-1.0]])],"derivedFrom":subQ0}),makeQuery(id+"F0.imprint","IMPRINT",EDGE,{"disambiguationData":[TD([[subQ1,-1.0]])],"derivedFrom":subQ0}),makeQuery(id+"F0.imprint","IMPRINT",EDGE,{"disambiguationData":[TD([[subQ2,-1.0]])],"derivedFrom":subQ0})])],"isStart":false});}
            var Q29;
            Q29=makeQuery(id+"F1.opExtrude","CAP_EDGE",EDGE,{"disambiguationData":[OSD([sQuery(id+"F0.wireOp",EDGE,"E0")])],"isStart":false});
            var Q30;
            Q30=makeQuery(id+"F2.opExtrude","CAP_EDGE",EDGE,{"disambiguationData":[OSD([sQuery(id+"F0.wireOp",EDGE,"E23"),sQuery(id+"F0.wireOp",EDGE,"E35.MirrorCS")])],"isStart":false});
            var Q31;
            Q31=makeQuery(id+"F10.boolean.opBoolean","INTERSECT",EDGE,{"derivedFrom":[makeQuery(id+"F7.opExtrude","SWEPT_FACE",FACE,{"disambiguationData":[OSD([sQuery(id+"F6.wireOp",EDGE,"E51.0.1"),sQuery(id+"F6.wireOp",EDGE,"E51.0.2"),sQuery(id+"F6.wireOp",EDGE,"E51.0.3")])]}),makeQuery(id+"F10.opExtrude","SWEPT_FACE",FACE,{"disambiguationData":[OSD([sQuery(id+"F9.wireOp",EDGE,"E58")])]})]});
            var Q32;
            {var subQ0=sQuery(id+"F0.wireOp",EDGE,"E44");var subQ1=sQuery(id+"F0.wireOp",EDGE,"E47");Q32=makeQuery(id+"F3.boolean.opBoolean","MERGE",EDGE,{"derivedFrom":[makeQuery(id+"F2.opExtrude","SWEPT_EDGE",EDGE,{"disambiguationData":[OSD([subQ0,subQ1])]}),makeQuery(id+"F3.opExtrude","SWEPT_EDGE",EDGE,{"disambiguationData":[OSD([sQuery(id+"F0.wireOp",EDGE,"E0"),sQuery(id+"F0.wireOp",EDGE,"E3"),sQuery(id+"F0.wireOp",EDGE,"E6"),sQuery(id+"F0.wireOp",EDGE,"E7"),sQuery(id+"F0.wireOp",EDGE,"E10.MirrorCS"),sQuery(id+"F0.wireOp",EDGE,"E11.MirrorC"),sQuery(id+"F0.wireOp",EDGE,"E13.MirrorC"),sQuery(id+"F0.wireOp",EDGE,"E19"),sQuery(id+"F0.wireOp",EDGE,"E20"),sQuery(id+"F0.wireOp",EDGE,"E25.MirrorCS"),sQuery(id+"F0.wireOp",EDGE,"E28.MirrorCS"),sQuery(id+"F0.wireOp",EDGE,"E30.MirrorC"),sQuery(id+"F0.wireOp",EDGE,"E33.MirrorC"),sQuery(id+"F0.wireOp",EDGE,"E34.MirrorCS"),sQuery(id+"F0.wireOp",EDGE,"E39.MirrorCS"),sQuery(id+"F0.wireOp",EDGE,"E42.MirrorCS"),subQ0,sQuery(id+"F0.wireOp",EDGE,"E46"),subQ1,sQuery(id+"F0.wireOp",EDGE,"E48")])]})]});}
            var Q33;
            Q33=makeQuery(id+"F4.opExtrude","CAP_EDGE",EDGE,{"disambiguationData":[OSD([sQuery(id+"F0.wireOp",EDGE,"E25.MirrorCS")])],"isStart":false});
            var Q34;
            Q34=makeQuery(id+"F4.opExtrude","SWEPT_EDGE",EDGE,{"disambiguationData":[OSD([sQuery(id+"F0.wireOp",EDGE,"E25.MirrorCS"),sQuery(id+"F0.wireOp",EDGE,"E42.MirrorCS")])]});
            var Q35;
            Q35=makeQuery(id+"F2.opExtrude","SWEPT_EDGE",EDGE,{"disambiguationData":[OSD([sQuery(id+"F0.wireOp",EDGE,"E42.MirrorCS"),sQuery(id+"F0.wireOp",EDGE,"E45")])]});
            var Q36;
            {var subQ0=sQuery(id+"F0.wireOp",EDGE,"E42.MirrorCS");var subQ1=makeQuery(id+"F0.imprint","INTERSECT",VERTEX,{"derivedFrom":[subQ0,sQuery(id+"F0.wireOp",EDGE,"E44")]});Q36=makeQuery(id+"F2.opExtrude","CAP_EDGE",EDGE,{"disambiguationData":[OSD([subQ0]),TDD([makeQuery(id+"F0.imprint","IMPRINT",EDGE,{"disambiguationData":[TD([[makeQuery(id+"F0.imprint","INTERSECT",VERTEX,{"derivedFrom":[sQuery(id+"F0.wireOp",EDGE,"E25.MirrorCS"),subQ0]}),-1.0]])],"derivedFrom":subQ0}),makeQuery(id+"F0.imprint","IMPRINT",EDGE,{"disambiguationData":[TD([[subQ1,-1.0]])],"derivedFrom":subQ0})])],"isStart":false});}
            var Q37;
            {var subQ0=sQuery(id+"F0.wireOp",EDGE,"E47");var subQ1=sQuery(id+"F9.wireOp",EDGE,"E60.trimOffspring");Q37=makeQuery(id+"F10.boolean.opBoolean","INTERSECT",EDGE,{"derivedFrom":[makeQuery(id+"F7.boolean.opBoolean","MERGE",FACE,{"derivedFrom":[makeQuery(id+"F3.boolean.opBoolean","MERGE",FACE,{"derivedFrom":[makeQuery(id+"F2.opExtrude","SWEPT_FACE",FACE,{"disambiguationData":[OSD([subQ0])]}),makeQuery(id+"F3.opExtrude","SWEPT_FACE",FACE,{"disambiguationData":[OSD([sQuery(id+"F0.wireOp",EDGE,"E0"),sQuery(id+"F0.wireOp",EDGE,"E3"),sQuery(id+"F0.wireOp",EDGE,"E6"),sQuery(id+"F0.wireOp",EDGE,"E7"),sQuery(id+"F0.wireOp",EDGE,"E10.MirrorCS"),sQuery(id+"F0.wireOp",EDGE,"E11.MirrorC"),sQuery(id+"F0.wireOp",EDGE,"E13.MirrorC"),sQuery(id+"F0.wireOp",EDGE,"E19"),sQuery(id+"F0.wireOp",EDGE,"E20"),sQuery(id+"F0.wireOp",EDGE,"E25.MirrorCS"),sQuery(id+"F0.wireOp",EDGE,"E28.MirrorCS"),sQuery(id+"F0.wireOp",EDGE,"E30.MirrorC"),sQuery(id+"F0.wireOp",EDGE,"E33.MirrorC"),sQuery(id+"F0.wireOp",EDGE,"E34.MirrorCS"),sQuery(id+"F0.wireOp",EDGE,"E39.MirrorCS"),sQuery(id+"F0.wireOp",EDGE,"E42.MirrorCS"),sQuery(id+"F0.wireOp",EDGE,"E46"),subQ0,sQuery(id+"F0.wireOp",EDGE,"E48")])]})]}),makeQuery(id+"F7.opExtrude","SWEPT_FACE",FACE,{"disambiguationData":[OSD([sQuery(id+"F6.wireOp",EDGE,"E51.0.5")])]})]}),makeQuery(id+"F10.opExtrude","SWEPT_FACE",FACE,{"disambiguationData":[OSD([subQ1]),TDD([makeQuery(id+"F9.imprint","IMPRINT",EDGE,{"disambiguationData":[TD([[makeQuery(id+"F9.imprint","INTERSECT",VERTEX,{"derivedFrom":[sQuery(id+"F9.wireOp",EDGE,"E59"),subQ1]}),-1.0]])],"derivedFrom":subQ1})])]}),makeQuery(id+"F10.opExtrude","SWEPT_FACE",FACE,{"disambiguationData":[OSD([subQ1]),TDD([makeQuery(id+"F9.imprint","IMPRINT",EDGE,{"disambiguationData":[TD([[makeQuery(id+"F9.imprint","INTERSECT",VERTEX,{"derivedFrom":[sQuery(id+"F9.wireOp",EDGE,"E58"),subQ1]}),1.0]])],"derivedFrom":subQ1})])]})]});}
            var Q38;
            {var subQ0=sQuery(id+"F6.wireOp",EDGE,"E51.0.1");var subQ1=sQuery(id+"F6.wireOp",EDGE,"E51.0.2");var subQ2=sQuery(id+"F6.wireOp",EDGE,"E51.0.3");var subQ3=sQuery(id+"F0.wireOp",EDGE,"E20");Q38=makeQuery(id+"F7.boolean.opBoolean","SPLIT",EDGE,{"disambiguationData":[TD([makeQuery(id+"F4.opExtrude","SWEPT_FACE",FACE,{"disambiguationData":[OSD([subQ3])]})])],"derivedFrom":makeQuery(id+"F7.opExtrude","CAP_EDGE",EDGE,{"disambiguationData":[OSD([subQ0,subQ1,subQ2])],"isStart":true})});}
            var Q39;
            Q39=makeQuery(id+"F4.opExtrude","CAP_EDGE",EDGE,{"disambiguationData":[OSD([sQuery(id+"F0.wireOp",EDGE,"E46")])],"isStart":false});
            var Q40;
            Q40=makeQuery(id+"F4.opExtrude","CAP_EDGE",EDGE,{"disambiguationData":[OSD([sQuery(id+"F0.wireOp",EDGE,"E48")])],"isStart":false});
            var Q41;
            Q41=makeQuery(id+"F4.opExtrude","SWEPT_EDGE",EDGE,{"disambiguationData":[OSD([sQuery(id+"F0.wireOp",EDGE,"E19"),sQuery(id+"F0.wireOp",EDGE,"E46")])]});
            var Q42;
            Q42=makeQuery(id+"F4.opExtrude","SWEPT_EDGE",EDGE,{"disambiguationData":[OSD([sQuery(id+"F0.wireOp",EDGE,"E20"),sQuery(id+"F0.wireOp",EDGE,"E46")])]});
            var Q43;
            Q43=makeQuery(id+"F4.opExtrude","SWEPT_EDGE",EDGE,{"disambiguationData":[OSD([sQuery(id+"F0.wireOp",EDGE,"E25.MirrorCS"),sQuery(id+"F0.wireOp",EDGE,"E48")])]});
            var Q44;
            {var subQ0=sQuery(id+"F6.wireOp",EDGE,"E51.0.1");var subQ1=sQuery(id+"F6.wireOp",EDGE,"E51.0.2");var subQ2=sQuery(id+"F6.wireOp",EDGE,"E51.0.3");var subQ3=sQuery(id+"F0.wireOp",EDGE,"E19");Q44=makeQuery(id+"F7.boolean.opBoolean","SPLIT",EDGE,{"disambiguationData":[TD([makeQuery(id+"F4.opExtrude","SWEPT_FACE",FACE,{"disambiguationData":[OSD([subQ3])]})])],"derivedFrom":makeQuery(id+"F7.opExtrude","CAP_EDGE",EDGE,{"disambiguationData":[OSD([subQ0,subQ1,subQ2])],"isStart":true})});}
            var Q45;
            {var subQ0=sQuery(id+"F0.wireOp",EDGE,"E47");Q45=makeQuery(id+"F10.boolean.opBoolean","INTERSECT",EDGE,{"derivedFrom":[makeQuery(id+"F7.boolean.opBoolean","MERGE",FACE,{"derivedFrom":[makeQuery(id+"F3.boolean.opBoolean","MERGE",FACE,{"derivedFrom":[makeQuery(id+"F2.opExtrude","SWEPT_FACE",FACE,{"disambiguationData":[OSD([subQ0])]}),makeQuery(id+"F3.opExtrude","SWEPT_FACE",FACE,{"disambiguationData":[OSD([sQuery(id+"F0.wireOp",EDGE,"E0"),sQuery(id+"F0.wireOp",EDGE,"E3"),sQuery(id+"F0.wireOp",EDGE,"E6"),sQuery(id+"F0.wireOp",EDGE,"E7"),sQuery(id+"F0.wireOp",EDGE,"E10.MirrorCS"),sQuery(id+"F0.wireOp",EDGE,"E11.MirrorC"),sQuery(id+"F0.wireOp",EDGE,"E13.MirrorC"),sQuery(id+"F0.wireOp",EDGE,"E19"),sQuery(id+"F0.wireOp",EDGE,"E20"),sQuery(id+"F0.wireOp",EDGE,"E25.MirrorCS"),sQuery(id+"F0.wireOp",EDGE,"E28.MirrorCS"),sQuery(id+"F0.wireOp",EDGE,"E30.MirrorC"),sQuery(id+"F0.wireOp",EDGE,"E33.MirrorC"),sQuery(id+"F0.wireOp",EDGE,"E34.MirrorCS"),sQuery(id+"F0.wireOp",EDGE,"E39.MirrorCS"),sQuery(id+"F0.wireOp",EDGE,"E42.MirrorCS"),sQuery(id+"F0.wireOp",EDGE,"E46"),subQ0,sQuery(id+"F0.wireOp",EDGE,"E48")])]})]}),makeQuery(id+"F7.opExtrude","SWEPT_FACE",FACE,{"disambiguationData":[OSD([sQuery(id+"F6.wireOp",EDGE,"E51.0.5")])]})]}),makeQuery(id+"F10.opExtrude","SWEPT_FACE",FACE,{"disambiguationData":[OSD([sQuery(id+"F9.wireOp",EDGE,"E58")])]})]});}
            var Q46;
            Q46=makeQuery(id+"F10.boolean.opBoolean","MERGE",EDGE,{"derivedFrom":[makeQuery(id+"F7.opExtrude","CAP_EDGE",EDGE,{"disambiguationData":[OSD([sQuery(id+"F6.wireOp",EDGE,"E51.0.0")])],"isStart":true}),makeQuery(id+"F10.opExtrude","SWEPT_EDGE",EDGE,{"disambiguationData":[OSD([sQuery(id+"F9.wireOp",EDGE,"E54.0.4"),sQuery(id+"F9.wireOp",EDGE,"E59"),sQuery(id+"F9.wireOp",EDGE,"E54.0.5")])]})]});
            var Q47;
            Q47=makeQuery(id+"F10.boolean.opBoolean","MERGE",EDGE,{"derivedFrom":[makeQuery(id+"F7.opExtrude","CAP_EDGE",EDGE,{"disambiguationData":[OSD([sQuery(id+"F6.wireOp",EDGE,"E51.0.4")])],"isStart":true}),makeQuery(id+"F10.opExtrude","SWEPT_EDGE",EDGE,{"disambiguationData":[OSD([sQuery(id+"F9.wireOp",EDGE,"E54.0.0"),sQuery(id+"F9.wireOp",EDGE,"E58"),sQuery(id+"F9.wireOp",EDGE,"E61")])]})]});
            var Q48;
            {var subQ0=sQuery(id+"F0.wireOp",EDGE,"E3");var subQ1=makeQuery(id+"F0.imprint","INTERSECT",VERTEX,{"derivedFrom":[subQ0,sQuery(id+"F0.wireOp",EDGE,"E44")]});Q48=makeQuery(id+"F2.opExtrude","CAP_EDGE",EDGE,{"disambiguationData":[OSD([subQ0]),TDD([makeQuery(id+"F0.imprint","IMPRINT",EDGE,{"disambiguationData":[TD([[makeQuery(id+"F0.imprint","INTERSECT",VERTEX,{"derivedFrom":[subQ0,sQuery(id+"F0.wireOp",EDGE,"E20")]}),-1.0]])],"derivedFrom":subQ0}),makeQuery(id+"F0.imprint","IMPRINT",EDGE,{"disambiguationData":[TD([[subQ1,-1.0]])],"derivedFrom":subQ0})])],"isStart":false});}
            var Q49;
            Q49=makeQuery(id+"F2.opExtrude","SWEPT_EDGE",EDGE,{"disambiguationData":[OSD([sQuery(id+"F0.wireOp",EDGE,"E3"),sQuery(id+"F0.wireOp",EDGE,"E24")])]});
            var Q50;
            Q50=makeQuery(id+"F10.boolean.opBoolean","COPY",EDGE,{"disambiguationData":[OD(1.0)],"derivedFrom":makeQuery(id+"F10.opExtrude","SWEPT_EDGE",EDGE,{"disambiguationData":[OSD([sQuery(id+"F9.wireOp",EDGE,"E58"),sQuery(id+"F9.wireOp",EDGE,"E60.trimOffspring")])]})});
            var Q51;
            {var subQ0=sQuery(id+"F0.wireOp",EDGE,"E42.MirrorCS");Q51=makeQuery(id+"F2.opExtrude","CAP_EDGE",EDGE,{"disambiguationData":[OSD([subQ0]),TDD([makeQuery(id+"F0.imprint","IMPRINT",EDGE,{"disambiguationData":[TD([[makeQuery(id+"F0.imprint","INTERSECT",VERTEX,{"derivedFrom":[sQuery(id+"F0.wireOp",EDGE,"E32.MirrorCS"),subQ0]}),-1.0]])],"derivedFrom":subQ0}),makeQuery(id+"F0.imprint","IMPRINT",EDGE,{"disambiguationData":[TD([[makeQuery(id+"F0.imprint","INTERSECT",VERTEX,{"derivedFrom":[sQuery(id+"F0.wireOp",EDGE,"E28.MirrorCS"),subQ0]}),1.0]])],"derivedFrom":subQ0})])],"isStart":false});}
            var Q52;
            Q52=makeQuery(id+"F2.boolean.opBoolean","INTERSECT",EDGE,{"derivedFrom":[makeQuery(id+"F1.opExtrude","CAP_FACE",FACE,{"disambiguationData":[OSD([sQuery(id+"F0.wireOp",EDGE,"E0"),sQuery(id+"F0.wireOp",EDGE,"E3"),sQuery(id+"F0.wireOp",EDGE,"E6"),sQuery(id+"F0.wireOp",EDGE,"E7"),sQuery(id+"F0.wireOp",EDGE,"E10.MirrorCS"),sQuery(id+"F0.wireOp",EDGE,"E11.MirrorC"),sQuery(id+"F0.wireOp",EDGE,"E13.MirrorC"),sQuery(id+"F0.wireOp",EDGE,"E19"),sQuery(id+"F0.wireOp",EDGE,"E20"),sQuery(id+"F0.wireOp",EDGE,"E25.MirrorCS"),sQuery(id+"F0.wireOp",EDGE,"E28.MirrorCS"),sQuery(id+"F0.wireOp",EDGE,"E30.MirrorC"),sQuery(id+"F0.wireOp",EDGE,"E33.MirrorC"),sQuery(id+"F0.wireOp",EDGE,"E34.MirrorCS"),sQuery(id+"F0.wireOp",EDGE,"E39.MirrorCS"),sQuery(id+"F0.wireOp",EDGE,"E42.MirrorCS"),sQuery(id+"F0.wireOp",EDGE,"E46"),sQuery(id+"F0.wireOp",EDGE,"E48")])],"isStart":false}),makeQuery(id+"F2.opExtrude","SWEPT_FACE",FACE,{"disambiguationData":[OSD([sQuery(id+"F0.wireOp",EDGE,"E24"),sQuery(id+"F0.wireOp",EDGE,"E32.MirrorCS")])]})]});
            var Q53;
            Q53=makeQuery(id+"F2.opExtrude","SWEPT_EDGE",EDGE,{"disambiguationData":[OSD([sQuery(id+"F0.wireOp",EDGE,"E3"),sQuery(id+"F0.wireOp",EDGE,"E45")])]});
            var Q54;
            Q54=makeQuery(id+"F10.boolean.opBoolean","COPY",EDGE,{"disambiguationData":[OD(0.0)],"derivedFrom":makeQuery(id+"F10.opExtrude","SWEPT_EDGE",EDGE,{"disambiguationData":[OSD([sQuery(id+"F9.wireOp",EDGE,"E59"),sQuery(id+"F9.wireOp",EDGE,"E60.trimOffspring")])]})});
            var Q55;
            {var subQ0=sQuery(id+"F0.wireOp",EDGE,"E3");var subQ2=makeQuery(id+"F0.imprint","INTERSECT",VERTEX,{"derivedFrom":[subQ0,sQuery(id+"F0.wireOp",EDGE,"E23")]});Q55=makeQuery(id+"F1.opExtrude","CAP_EDGE",EDGE,{"disambiguationData":[OSD([subQ0]),TDD([makeQuery(id+"F0.imprint","IMPRINT",EDGE,{"disambiguationData":[TD([[makeQuery(id+"F0.imprint","INTERSECT",VERTEX,{"derivedFrom":[sQuery(id+"F0.wireOp",EDGE,"E0"),subQ0]}),-1.0]])],"derivedFrom":subQ0}),makeQuery(id+"F0.imprint","IMPRINT",EDGE,{"disambiguationData":[TD([[subQ2,1.0]])],"derivedFrom":subQ0}),makeQuery(id+"F0.imprint","IMPRINT",EDGE,{"disambiguationData":[TD([[makeQuery(id+"F0.imprint","INTERSECT",VERTEX,{"derivedFrom":[subQ0,sQuery(id+"F0.wireOp",EDGE,"E19")]}),1.0]])],"derivedFrom":subQ0})])],"isStart":false});}
            var Q56;
            {var subQ0=sQuery(id+"F0.wireOp",EDGE,"E3");var subQ1=makeQuery(id+"F0.imprint","INTERSECT",VERTEX,{"derivedFrom":[subQ0,sQuery(id+"F0.wireOp",EDGE,"E44")]});Q56=makeQuery(id+"F1.opExtrude","CAP_EDGE",EDGE,{"disambiguationData":[OSD([subQ0]),TDD([makeQuery(id+"F0.imprint","IMPRINT",EDGE,{"disambiguationData":[TD([[makeQuery(id+"F0.imprint","INTERSECT",VERTEX,{"derivedFrom":[subQ0,sQuery(id+"F0.wireOp",EDGE,"E20")]}),-1.0]])],"derivedFrom":subQ0}),makeQuery(id+"F0.imprint","IMPRINT",EDGE,{"disambiguationData":[TD([[subQ1,-1.0]])],"derivedFrom":subQ0}),makeQuery(id+"F0.imprint","IMPRINT",EDGE,{"disambiguationData":[TD([[makeQuery(id+"F0.imprint","INTERSECT",VERTEX,{"derivedFrom":[subQ0,sQuery(id+"F0.wireOp",EDGE,"E11.MirrorC")]}),1.0]])],"derivedFrom":subQ0})])],"isStart":false});}
            var Q57;
            {var subQ0=sQuery(id+"F0.wireOp",EDGE,"E23");var subQ1=sQuery(id+"F0.wireOp",EDGE,"E47");Q57=makeQuery(id+"F3.boolean.opBoolean","MERGE",EDGE,{"derivedFrom":[makeQuery(id+"F2.opExtrude","SWEPT_EDGE",EDGE,{"disambiguationData":[OSD([subQ0,subQ1])]}),makeQuery(id+"F3.opExtrude","SWEPT_EDGE",EDGE,{"disambiguationData":[OSD([sQuery(id+"F0.wireOp",EDGE,"E0"),sQuery(id+"F0.wireOp",EDGE,"E3"),sQuery(id+"F0.wireOp",EDGE,"E6"),sQuery(id+"F0.wireOp",EDGE,"E7"),sQuery(id+"F0.wireOp",EDGE,"E10.MirrorCS"),sQuery(id+"F0.wireOp",EDGE,"E11.MirrorC"),sQuery(id+"F0.wireOp",EDGE,"E13.MirrorC"),sQuery(id+"F0.wireOp",EDGE,"E19"),sQuery(id+"F0.wireOp",EDGE,"E20"),subQ0,sQuery(id+"F0.wireOp",EDGE,"E25.MirrorCS"),sQuery(id+"F0.wireOp",EDGE,"E28.MirrorCS"),sQuery(id+"F0.wireOp",EDGE,"E30.MirrorC"),sQuery(id+"F0.wireOp",EDGE,"E33.MirrorC"),sQuery(id+"F0.wireOp",EDGE,"E34.MirrorCS"),sQuery(id+"F0.wireOp",EDGE,"E35.MirrorCS"),sQuery(id+"F0.wireOp",EDGE,"E39.MirrorCS"),sQuery(id+"F0.wireOp",EDGE,"E42.MirrorCS"),sQuery(id+"F0.wireOp",EDGE,"E46"),subQ1,sQuery(id+"F0.wireOp",EDGE,"E48")])]})]});}
            var Q58;
            {var subQ0=sQuery(id+"F0.wireOp",EDGE,"E35.MirrorCS");var subQ1=sQuery(id+"F0.wireOp",EDGE,"E49");Q58=makeQuery(id+"F3.boolean.opBoolean","MERGE",EDGE,{"derivedFrom":[makeQuery(id+"F2.opExtrude","SWEPT_EDGE",EDGE,{"disambiguationData":[OSD([subQ0,subQ1])]}),makeQuery(id+"F3.opExtrude","SWEPT_EDGE",EDGE,{"disambiguationData":[OSD([sQuery(id+"F0.wireOp",EDGE,"E0"),sQuery(id+"F0.wireOp",EDGE,"E3"),sQuery(id+"F0.wireOp",EDGE,"E6"),sQuery(id+"F0.wireOp",EDGE,"E7"),sQuery(id+"F0.wireOp",EDGE,"E10.MirrorCS"),sQuery(id+"F0.wireOp",EDGE,"E11.MirrorC"),sQuery(id+"F0.wireOp",EDGE,"E13.MirrorC"),sQuery(id+"F0.wireOp",EDGE,"E19"),sQuery(id+"F0.wireOp",EDGE,"E20"),sQuery(id+"F0.wireOp",EDGE,"E23"),sQuery(id+"F0.wireOp",EDGE,"E25.MirrorCS"),sQuery(id+"F0.wireOp",EDGE,"E28.MirrorCS"),sQuery(id+"F0.wireOp",EDGE,"E30.MirrorC"),sQuery(id+"F0.wireOp",EDGE,"E33.MirrorC"),sQuery(id+"F0.wireOp",EDGE,"E34.MirrorCS"),subQ0,sQuery(id+"F0.wireOp",EDGE,"E39.MirrorCS"),sQuery(id+"F0.wireOp",EDGE,"E42.MirrorCS"),sQuery(id+"F0.wireOp",EDGE,"E46"),sQuery(id+"F0.wireOp",EDGE,"E48"),subQ1])]})]});}
            var Q59;
            {var subQ0=sQuery(id+"F0.wireOp",EDGE,"E44");var subQ1=sQuery(id+"F0.wireOp",EDGE,"E49");Q59=makeQuery(id+"F3.boolean.opBoolean","MERGE",EDGE,{"derivedFrom":[makeQuery(id+"F2.opExtrude","SWEPT_EDGE",EDGE,{"disambiguationData":[OSD([subQ0,subQ1])]}),makeQuery(id+"F3.opExtrude","SWEPT_EDGE",EDGE,{"disambiguationData":[OSD([sQuery(id+"F0.wireOp",EDGE,"E0"),sQuery(id+"F0.wireOp",EDGE,"E3"),sQuery(id+"F0.wireOp",EDGE,"E6"),sQuery(id+"F0.wireOp",EDGE,"E7"),sQuery(id+"F0.wireOp",EDGE,"E10.MirrorCS"),sQuery(id+"F0.wireOp",EDGE,"E11.MirrorC"),sQuery(id+"F0.wireOp",EDGE,"E13.MirrorC"),sQuery(id+"F0.wireOp",EDGE,"E19"),sQuery(id+"F0.wireOp",EDGE,"E20"),sQuery(id+"F0.wireOp",EDGE,"E25.MirrorCS"),sQuery(id+"F0.wireOp",EDGE,"E28.MirrorCS"),sQuery(id+"F0.wireOp",EDGE,"E30.MirrorC"),sQuery(id+"F0.wireOp",EDGE,"E33.MirrorC"),sQuery(id+"F0.wireOp",EDGE,"E34.MirrorCS"),sQuery(id+"F0.wireOp",EDGE,"E39.MirrorCS"),sQuery(id+"F0.wireOp",EDGE,"E42.MirrorCS"),subQ0,sQuery(id+"F0.wireOp",EDGE,"E46"),sQuery(id+"F0.wireOp",EDGE,"E48"),subQ1])]})]});}
            var Q60;
            Q60=makeQuery(id+"F4.opExtrude","CAP_EDGE",EDGE,{"disambiguationData":[OSD([sQuery(id+"F0.wireOp",EDGE,"E20")])],"isStart":false});
            var Q61;
            Q61=makeQuery(id+"F4.opExtrude","SWEPT_EDGE",EDGE,{"disambiguationData":[OSD([sQuery(id+"F0.wireOp",EDGE,"E28.MirrorCS"),sQuery(id+"F0.wireOp",EDGE,"E42.MirrorCS")])]});
            var Q62;
            Q62=makeQuery(id+"F4.opExtrude","CAP_EDGE",EDGE,{"disambiguationData":[OSD([sQuery(id+"F0.wireOp",EDGE,"E3")])],"isStart":false});
            var Q63;
            Q63=makeQuery(id+"F2.opExtrude","CAP_EDGE",EDGE,{"disambiguationData":[OSD([sQuery(id+"F0.wireOp",EDGE,"E20")])],"isStart":false});
            var Q64;
            Q64=makeQuery(id+"F2.opExtrude","CAP_EDGE",EDGE,{"disambiguationData":[OSD([sQuery(id+"F0.wireOp",EDGE,"E25.MirrorCS")])],"isStart":false});
            var Q65;
            Q65=makeQuery(id+"F2.opExtrude","CAP_EDGE",EDGE,{"disambiguationData":[OSD([sQuery(id+"F0.wireOp",EDGE,"E28.MirrorCS")])],"isStart":false});
            var Q66;
            Q66=makeQuery(id+"F10.boolean.opBoolean","COPY",EDGE,{"disambiguationData":[OD(1.0)],"derivedFrom":makeQuery(id+"F10.opExtrude","SWEPT_EDGE",EDGE,{"disambiguationData":[OSD([sQuery(id+"F9.wireOp",EDGE,"E59"),sQuery(id+"F9.wireOp",EDGE,"E60.trimOffspring")])]})});
            var Q67;
            Q67=makeQuery(id+"F4.opExtrude","SWEPT_EDGE",EDGE,{"disambiguationData":[OSD([sQuery(id+"F0.wireOp",EDGE,"E3"),sQuery(id+"F0.wireOp",EDGE,"E19")])]});
            var Q68;
            Q68=makeQuery(id+"F2.boolean.opBoolean","INTERSECT",EDGE,{"derivedFrom":[makeQuery(id+"F1.opExtrude","CAP_FACE",FACE,{"disambiguationData":[OSD([sQuery(id+"F0.wireOp",EDGE,"E0"),sQuery(id+"F0.wireOp",EDGE,"E3"),sQuery(id+"F0.wireOp",EDGE,"E6"),sQuery(id+"F0.wireOp",EDGE,"E7"),sQuery(id+"F0.wireOp",EDGE,"E10.MirrorCS"),sQuery(id+"F0.wireOp",EDGE,"E11.MirrorC"),sQuery(id+"F0.wireOp",EDGE,"E13.MirrorC"),sQuery(id+"F0.wireOp",EDGE,"E19"),sQuery(id+"F0.wireOp",EDGE,"E20"),sQuery(id+"F0.wireOp",EDGE,"E25.MirrorCS"),sQuery(id+"F0.wireOp",EDGE,"E28.MirrorCS"),sQuery(id+"F0.wireOp",EDGE,"E30.MirrorC"),sQuery(id+"F0.wireOp",EDGE,"E33.MirrorC"),sQuery(id+"F0.wireOp",EDGE,"E34.MirrorCS"),sQuery(id+"F0.wireOp",EDGE,"E39.MirrorCS"),sQuery(id+"F0.wireOp",EDGE,"E42.MirrorCS"),sQuery(id+"F0.wireOp",EDGE,"E46"),sQuery(id+"F0.wireOp",EDGE,"E48")])],"isStart":false}),makeQuery(id+"F2.opExtrude","SWEPT_FACE",FACE,{"disambiguationData":[OSD([sQuery(id+"F0.wireOp",EDGE,"E45")])]})]});
            var Q69;
            Q69=makeQuery(id+"F2.opExtrude","CAP_EDGE",EDGE,{"disambiguationData":[OSD([sQuery(id+"F0.wireOp",EDGE,"E19")])],"isStart":false});
            var Q70;
            Q70=makeQuery(id+"F4.opExtrude","CAP_EDGE",EDGE,{"disambiguationData":[OSD([sQuery(id+"F0.wireOp",EDGE,"E19")])],"isStart":false});
            var Q71;
            Q71=makeQuery(id+"F4.opExtrude","SWEPT_EDGE",EDGE,{"disambiguationData":[OSD([sQuery(id+"F0.wireOp",EDGE,"E3"),sQuery(id+"F0.wireOp",EDGE,"E20")])]});
            fillet(context, id + "F11", {"entities" : qUnion([Q0, Q1, Q2, Q3, Q4, Q5, Q6, Q7, Q8, Q9, Q10, Q11, Q12, Q13, Q14, Q15, Q16, Q17, Q18, Q19, Q20, Q21, Q22, Q23, Q24, Q25, Q26, Q27, Q28, Q29, Q30, Q31, Q32, Q33, Q34, Q35, Q36, Q37, Q38, Q39, Q40, Q41, Q42, Q43, Q44, Q45, Q46, Q47, Q48, Q49, Q50, Q51, Q52, Q53, Q54, Q55, Q56, Q57, Q58, Q59, Q60, Q61, Q62, Q63, Q64, Q65, Q66, Q67, Q68, Q69, Q70, Q71]), "radius" : 1.59 * mm, "tangentPropagation" : true, "allowEdgeOverflow" : false});
        }
    });
